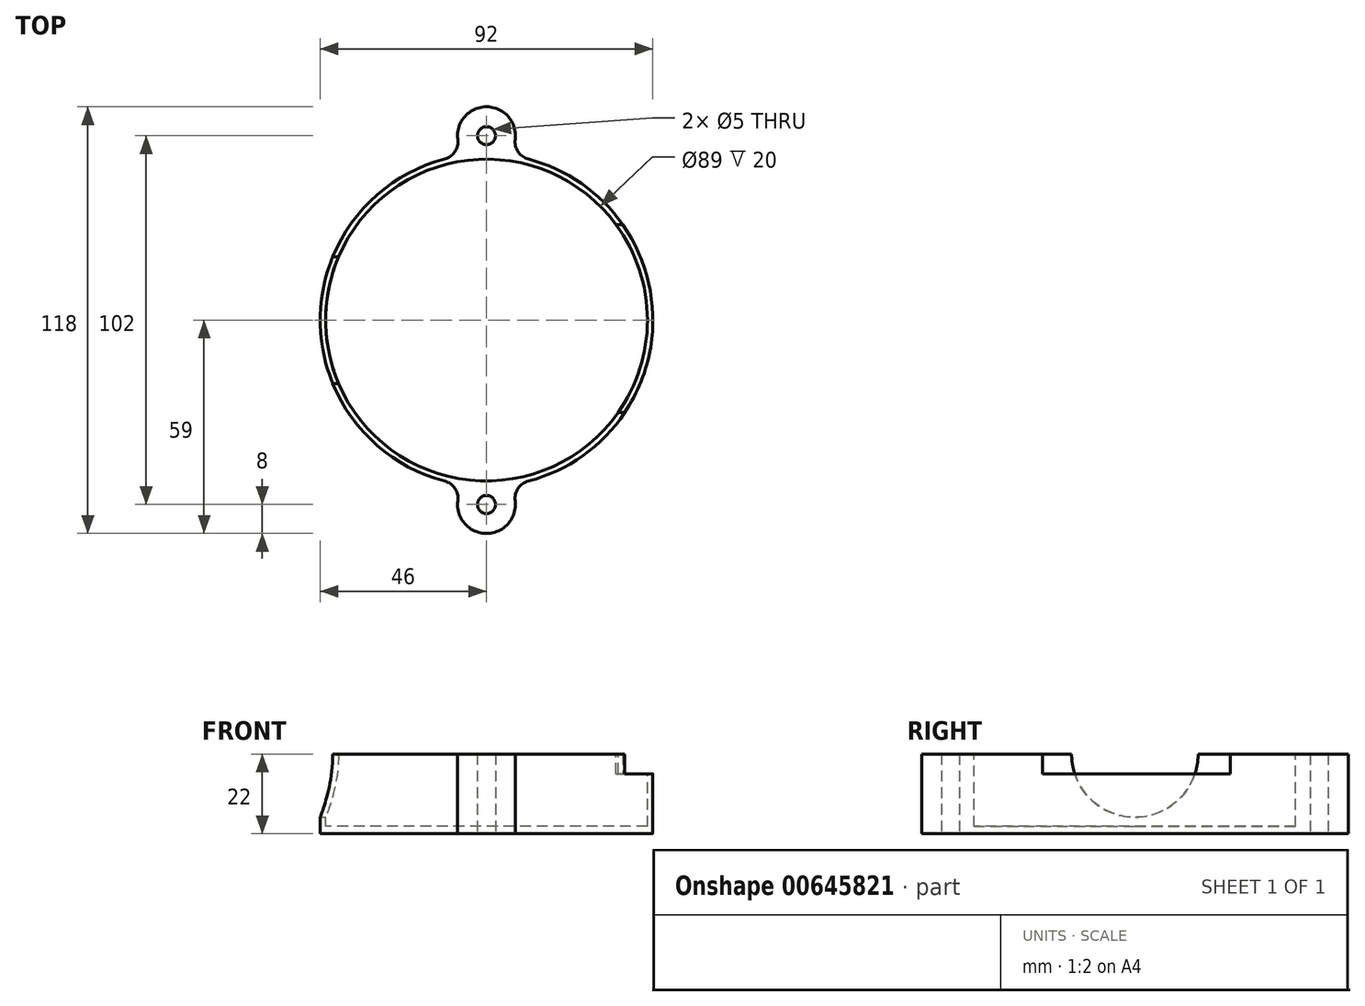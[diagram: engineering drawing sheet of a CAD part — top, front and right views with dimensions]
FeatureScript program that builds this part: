
annotation { "Feature Type Name" : "Feature", "Feature Type Description" : "" }
export const myFeature = defineFeature(function(context is Context, id is Id, definition is map)
    precondition{}
    {
        {
            var Q0;
            Q0=qCreatedBy(makeId("Top.planeOp"),FACE);
            var sketch = newSketch(context, id + "F0", { "sketchPlane" : qUnion([Q0])});
            skArc(sketch, "E0", {"start": v(45.39, -7.5) * mm, "mid": v(36.92, 27.44) * mm, "end": v(5.92, 45.62) * mm});
            skLineSegment(sketch, "E1", {"start": v(45.38, -7.5) * mm, "end": v(45.39, -7.5) * mm});
            skPoint(sketch, "E2", {"position": v(0, 51) * mm});
            skCircle(sketch, "E3", {"center": v(0, 51) * mm, "radius": 2.5 * mm});
            skArc(sketch, "E4", {"start": v(5.92, 45.62) * mm, "mid": v(0, 59) * mm, "end": v(-5.92, 45.62) * mm});
            skLineSegment(sketch, "E5", {"start": v(-59.66, 0) * mm, "end": v(61.44, 0) * mm, "construction": true});
            skArc(sketch, "E6.trimOffspring", {"start": v(-5.92, 45.62) * mm, "mid": v(-46, 0) * mm, "end": v(-5.92, -45.62) * mm});
            skArc(sketch, "E7.MirrorCS", {"start": v(5.92, -45.62) * mm, "mid": v(0, -59) * mm, "end": v(-5.92, -45.62) * mm});
            skCircle(sketch, "E8.MirrorC", {"center": v(0, -51) * mm, "radius": 2.5 * mm});
            skArc(sketch, "E9.trimOffspring", {"start": v(5.92, -45.62) * mm, "mid": v(31.96, -33.09) * mm, "end": v(45.38, -7.5) * mm});
            skSolve(sketch);
        }
        {
            var Q0;
            Q0 = qSketchRegion(id + "F0", true);
            extrude(context, id + "F1", {"entities" : qUnion([Q0]), "depth" : 22 * mm, "offsetDistance" : 25 * mm});
        }
        {
            var Q0;
            Q0=qCreatedBy(makeId("Right.planeOp"),FACE);
            var sketch = newSketch(context, id + "F2", { "sketchPlane" : qUnion([Q0])});
            skLineSegment(sketch, "E10", {"start": v(0, 0) * mm, "end": v(0, 22) * mm, "construction": true});
            skCircle(sketch, "E11", {"center": v(0, 22) * mm, "radius": 17.5 * mm});
            skSolve(sketch);
        }
        {
            var Q0;
            Q0=qCreatedBy(makeId("Right.planeOp"),FACE);
            var sketch = newSketch(context, id + "F3", { "sketchPlane" : qUnion([Q0])});
            skLineSegment(sketch, "E12.bottom", {"start": v(26.42, 22) * mm, "end": v(-25.58, 22) * mm});
            skLineSegment(sketch, "E12.top", {"start": v(26.42, 16.5) * mm, "end": v(-25.58, 16.5) * mm});
            skLineSegment(sketch, "E12.left", {"start": v(26.42, 22) * mm, "end": v(26.42, 16.5) * mm});
            skLineSegment(sketch, "E12.right", {"start": v(-25.58, 22) * mm, "end": v(-25.58, 16.5) * mm});
            skSolve(sketch);
        }
        {
            var Q0;
            Q0=makeQuery(id+"F3.imprint","IMPRINT",FACE,{"disambiguationData":[TD([[makeQuery(id+"F3.imprint","IMPRINT",EDGE,{"derivedFrom":sQuery(id+"F3.wireOp",EDGE,"E12.bottom")}),1.0]])]});
            extrude(context, id + "F4", {"entities" : qUnion([Q0]), "operationType" : NewBodyOperationType.REMOVE, "depth" : 115.14 * mm, "offsetDistance" : 25 * mm});
        }
        {
            var Q0;
            {var subQ0=sQuery(id+"F0.wireOp",EDGE,"E4");var subQ1=sQuery(id+"F0.wireOp",EDGE,"E1");var subQ2=sQuery(id+"F0.wireOp",EDGE,"E0");var subQ3=sQuery(id+"F0.wireOp",EDGE,"E3");Q0=makeQuery(id+"F4.boolean.opBoolean","SPLIT",FACE,{"disambiguationData":[TD([makeQuery(id+"F1.opExtrude","SWEPT_FACE",FACE,{"disambiguationData":[OSD([subQ3])]})])],"derivedFrom":makeQuery(id+"F1.opExtrude","CAP_FACE",FACE,{"disambiguationData":[OSD([subQ2,subQ1,subQ3,subQ0])],"isStart":false})});}
            var sketch = newSketch(context, id + "F5", { "sketchPlane" : qUnion([Q0])});
            skCircle(sketch, "E13", {"center": v(0, 0) * mm, "radius": 44.5 * mm});
            skSolve(sketch);
        }
        {
            var Q0;
            Q0 = qSketchRegion(id + "F5", true);
            extrude(context, id + "F6", {"entities" : qUnion([Q0]), "operationType" : NewBodyOperationType.REMOVE, "oppositeDirection" : true, "depth" : 20 * mm, "offsetDistance" : 25 * mm});
        }
        {
            var Q0;
            Q0=makeQuery(id+"F2.imprint","IMPRINT",FACE,{"disambiguationData":[TD([[makeQuery(id+"F2.imprint","IMPRINT",EDGE,{"derivedFrom":sQuery(id+"F2.wireOp",EDGE,"E11")}),1.0]])]});
            var Q1;
            Q1=sQuery(id+"F2.wireOp",EDGE,"E11");
            extrude(context, id + "F7", {"entities" : qUnion([Q0]), "operationType" : NewBodyOperationType.REMOVE, "surfaceEntities" : qUnion([Q1]), "oppositeDirection" : true, "depth" : 60.94 * mm, "offsetDistance" : 25 * mm});
        }
        {
            var Q0;
            Q0=makeQuery(id+"F1.opExtrude","SWEPT_EDGE",EDGE,{"disambiguationData":[OSD([sQuery(id+"F0.wireOp",EDGE,"E6.trimOffspring"),sQuery(id+"F0.wireOp",EDGE,"E7.MirrorCS")])]});
            var Q1;
            Q1=makeQuery(id+"F1.opExtrude","SWEPT_EDGE",EDGE,{"disambiguationData":[OSD([sQuery(id+"F0.wireOp",EDGE,"E7.MirrorCS"),sQuery(id+"F0.wireOp",EDGE,"E9.trimOffspring")])]});
            var Q2;
            Q2=makeQuery(id+"F1.opExtrude","SWEPT_EDGE",EDGE,{"disambiguationData":[OSD([sQuery(id+"F0.wireOp",EDGE,"E0"),sQuery(id+"F0.wireOp",EDGE,"E4")])]});
            var Q3;
            Q3=makeQuery(id+"F1.opExtrude","SWEPT_EDGE",EDGE,{"disambiguationData":[OSD([sQuery(id+"F0.wireOp",EDGE,"E4"),sQuery(id+"F0.wireOp",EDGE,"E6.trimOffspring")])]});
            fillet(context, id + "F8", {"entities" : qUnion([Q0, Q1, Q2, Q3]), "radius" : 5 * mm, "tangentPropagation" : true, "allowEdgeOverflow" : false});
        }
    });
